# Revit family: Windows_Purso_LK78_Triple-Sash_Inward-Opening-Window_68mm
name_source: partatom
category: Windows
revit_build: Autodesk Revit 2018 (Build: 20170223_1515(x64)
units: mm (PartAtom-declared; Revit-internal decimal feet)

## family parameters
Always vertical = Yes
Cut with Voids When Loaded = No
Host = Wall
OmniClass Number = 23.30.20.00
OmniClass Title = Windows
Room Calculation Point = No
Shared = No

## types (1)
- 2500mm x 1300mm
    Assembly Code = B2020100
    Default Sill Height = 800 mm  [stored 2.62467 ft]
    Description = LK78 Tripple Sash Inward Opening Window 68mm
    Edition number = 1
    Frame Material = Default
    Handle Material = Aluminium - Purso - Aluminium
    Height = 1300 mm
    Keynote = 08500
    Leaf Material = Default
    Manufacturer = Purso
    Model = LK78 Tripple Sash Inward Opening Window 68mm
    Product Guid = bbab472f-e2b9-4b89-aa6c-1e84ce4bab91
    Product data url = https://www.bimobject.com
    Type Comments = 2500mm x 1300mm
    URL = https://purso.fi
    Wall Closure = By host
    Width = 2500 mm  [stored 8.2021 ft]

note: [stored X ft] marks values corroborated as IEEE doubles in the binary element streams (Revit-internal decimal feet)

## geometry (parser evidence)
native form markers: Sweep x8
no freeform markers — native parametric forms only
